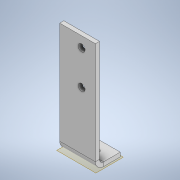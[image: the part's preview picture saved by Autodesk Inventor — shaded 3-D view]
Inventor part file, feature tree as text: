
AUTODESK INVENTOR PART (.ipt)
format: ipt  version: 2020 (Build 240168000, 168)  size: 184,832 bytes
history: native  units: in
note: dims shown in document units (in); Inventor stores cm internally (conversion verified against a paired STEP export)
features: sketch x4, sheet_metal_op x2, hole x2, other x2
ambient origin geometry x8: Origin, YZ Plane, XZ Plane, XY Plane, X Axis, Y Axis, Z Axis, Center Point
bodies: Solid1 (feature_tree)
feature tree (10):
  sheet_metal_op  "Face1"
  sheet_metal_op  "Fold1"
  hole  "Hole2"  [1 undecoded]
  hole  "Hole3"  [1 undecoded]
  sketch  "Sketch2"  dims[d6=0.1181in d9=0.1181in]
  other  "Plate1"
  sketch  "Sketch3"  dims[d10=0.0591in d11=0.2362in]
  sketch  "Sketch5"  dims[d12=0.1181in]
  sketch  "Sketch6"  dims[d13=90.0deg d14=0.1181in d34=0.2008in d35=0.1575in d36=0.3937in d37=0.2008in d38=0.2362in d39=0.1575in d40=0.0787in d41=90.0deg d42=0.315in d43=0.8108in d44=0.2008in d45=0.2008in d46=1.7717in d47=2.7559in d48=0.3937in d49=0.3937in d50=0.2008in d51=0.2362in d52=0.1575in d53=0.0787in d54=90.0deg d55=0.315in d56=0.8108in d57=0.5979in]
  other  "Definition1"
note: 2 required parameter values undecoded (feature->parameter linkage not recoverable at this tier; creation-order binding heuristic only, values carry confidence <= 0.55)
